FCSTD DOCUMENT  (FreeCAD 0.21R33694 (Git))
Label: boceto-carcasa
License: Creative Commons Attribution-NonCommercial-ShareAlike 4.0
LicenseURL: https://creativecommons.org/licenses/by-nc-sa/4.0/
objects: Part::Fuse×25, Part::Box×15, Part::Cut×15, Part::Feature×13, Part::Mirroring×13, Part::Cylinder×8, Sketcher::SketchObject×4, Part::Extrusion×4, Part::Chamfer×4, Part::Fillet×3, PartDesign::Body×2, Part::MultiFuse×2, App::LinkGroup×2, Mesh::Feature×1, PartDesign::Pad×1, Part::Compound×1
note: 111 computed .brp shape members not serialized (recipe doc carries the construction recipe); baked Part::Feature solids carry a one-line shape summary decoded from their .brp

FEATURE [Sketcher::SketchObject] Sketch  label="case-taladros"
  FullyConstrained = true
  MapMode = 5
  Support = -> [XY_Plane]
  sketch-geometry (8):
    g0: LineSegment StartX=-50 StartY=85 StartZ=0 EndX=50 EndY=85 EndZ=0
    g1: LineSegment StartX=50 StartY=85 StartZ=0 EndX=50 EndY=-85 EndZ=0
    g2: LineSegment StartX=50 StartY=-85 StartZ=0 EndX=-50 EndY=-85 EndZ=0
    g3: LineSegment StartX=-50 StartY=-85 StartZ=0 EndX=-50 EndY=85 EndZ=0
    g4: Circle CenterX=-40 CenterY=80 CenterZ=0 NormalX=0 NormalY=0 NormalZ=1 AngleXU=0 Radius=1.5
    g5: Circle CenterX=40 CenterY=80 CenterZ=0 NormalX=0 NormalY=0 NormalZ=1 AngleXU=0 Radius=1.5
    g6: Circle CenterX=40 CenterY=-80 CenterZ=0 NormalX=0 NormalY=0 NormalZ=1 AngleXU=0 Radius=1.5
    g7: Circle CenterX=-40 CenterY=-80 CenterZ=0 NormalX=0 NormalY=0 NormalZ=1 AngleXU=0 Radius=1.5
  constraints (19):
    c: Coincident(g0,g1)
    c: Coincident(g1,g2)
    c: Coincident(g2,g3)
    c: Coincident(g3,g0)
    c: Horizontal(g2)
    c: Vertical(g1)
    c: Symmetric(g0,g0,g-2)
    c: Symmetric(g2,g0,g-1)
    c: Equal(g4,g7)
    c: Equal(g7,g6)
    c: Equal(g6,g5)
    c: Symmetric(g7,g4,g-1)
    c: Symmetric(g4,g5,g-2)
    c: Symmetric(g6,g7,g-2)
    c: Diameter(g4) = 3
    c: DistanceY(g4,g0) = 5
    c: DistanceX(g0,g4) = 10
    c: DistanceY(g3,g3) = 170
    c: DistanceX(g0,g0) = 100
FEATURE [PartDesign::Body] Body  label="carcasa-boceto"
  Group = -> [Sketch]
  Origin = -> Origin
FEATURE [Part::Extrusion] Extrude  label="carcasa-extruida"
  Base = -> Sketch
  Dir = (0,0,1)
  DirMode = 2
  FaceMakerClass = Part::FaceMakerBullseye
  LengthFwd = 45
  LengthRev = 0
  Solid = true
  Symmetric = false
FEATURE [Part::Box] Box  label="llenado"
  AttacherType = Attacher::AttachEngine3D
  Height = 35
  Length = 100
  Placement = pos=(-50,-85,0) rot=(0,0,1;0rad)
  Width = 170
FEATURE [Part::Fuse] Fusion  label="carcasa-taladrada"
  Base = -> Extrude
  Refine = true
  Tool = -> Box
FEATURE [Part::Box] Box001  label="vaciado"
  AttacherType = Attacher::AttachEngine3D
  Height = 40
  Length = 80
  Placement = pos=(-40,-75,5) rot=(0,0,1;0rad)
  Width = 150
FEATURE [Part::Cut] Cut  label="carcasa-vaciada"
  Base = -> Fusion
  Refine = true
  Tool = -> Box001
FEATURE [Part::Fillet] Fillet
  Base = -> Cut
  Edges = 4 edges r=2: [Edge8,Edge9,Edge10,Edge11]
FEATURE [Part::Chamfer] Chamfer  label="carcasa001"
  Base = -> Fillet
  Edges = 4 edges r=2: [Edge5,Edge6,Edge7,Edge8]
FEATURE [Mesh::Feature] Arduino_Bumper_0005  label="Arduino-uno-case"
  Placement = pos=(-13,-40,5) rot=(0,0,1;-1.5708rad)
FEATURE [Part::Box] Box006  label="Cubo"
  AttacherType = Attacher::AttachEngine3D
  Height = 4
  Length = 50
  Placement = pos=(-25,22,-7.5) rot=(0,0,1;0rad)
  Width = 30
FEATURE [Part::Box] Box007  label="Cubo001"
  AttacherType = Attacher::AttachEngine3D
  Height = 20
  Length = 56
  Placement = pos=(-145,76,-21.5) rot=(0,0,1;0rad)
  Width = 16
FEATURE [Part::Cylinder] Cylinder001  label="cilindro-movil"
  Angle = 360
  AttacherType = Attacher::AttachEngine3D
  FirstAngle = 0
  Height = 170
  Placement = pos=(-200,92,-6) rot=(0,1,0;1.5708rad)
  Radius = 5
  SecondAngle = 0
FEATURE [Part::Feature] Fusion001005  label="Rosca macho006"
  Placement = pos=(-17,27,-10) rot=(0,0,1;0rad)
  shape: bbox 3.919 x 4.387 x 44 mm, 35 faces (baked)
FEATURE [Part::Feature] Fusion001006  label="Rosca macho007"
  Placement = pos=(17,27,-10) rot=(0,0,1;0rad)
  shape: bbox 3.919 x 4.387 x 44 mm, 35 faces (baked)
FEATURE [Part::MultiFuse] Fusion001007
  Refine = true
  Shapes = -> [Fusion001005,Fusion001006]
FEATURE [Part::Cut] Cut005  label="Soporte_eje"
  Base = -> Box006
  Placement = pos=(-117,36,0) rot=(0,0,1;0rad)
  Refine = true
  Tool = -> Fusion001007
FEATURE [Part::Feature] Fusion001008  label="Rosca macho008"
  Placement = pos=(-170,93.75,-8.78) rot=(0.819304,0.219813,-0.52955;0.936369rad)
  shape: bbox 4.221 x 33 x 32.52 mm, 35 faces (baked)
FEATURE [Part::Feature] Fusion001009  label="Rosca macho009"
  Placement = pos=(-60,93.75,-8.78) rot=(0.819304,0.219813,-0.52955;0.936369rad)
  shape: bbox 4.221 x 33 x 32.52 mm, 35 faces (baked)
FEATURE [Sketcher::SketchObject] Sketch007
  FullyConstrained = false
  MapMode = 5
  Placement = pos=(0,0,0) rot=(0.57735,0.57735,0.57735;2.0944rad)
  Support = -> [YZ_Plane003]
  sketch-geometry (6):
    g0: Circle CenterX=0 CenterY=0 CenterZ=0 NormalX=0 NormalY=0 NormalZ=1 AngleXU=0 Radius=8
    g1: Circle CenterX=0 CenterY=-1.19343 CenterZ=0 NormalX=0 NormalY=0 NormalZ=1 AngleXU=0 Radius=5.5
    g2: LineSegment StartX=-2.35964 StartY=6.31767 StartZ=0 EndX=2.35964 EndY=6.31767 EndZ=0
    g3: LineSegment StartX=2.35964 StartY=6.31767 StartZ=0 EndX=2.35964 EndY=5.38418 EndZ=0
    g4: LineSegment StartX=2.35964 StartY=5.38418 StartZ=0 EndX=-2.35964 EndY=5.38418 EndZ=0
    g5: LineSegment StartX=-2.35964 StartY=5.38418 StartZ=0 EndX=-2.35964 EndY=6.31767 EndZ=0
  constraints (12):
    c: Coincident(g0,g-1)
    c: Coincident(g2,g3)
    c: Coincident(g3,g4)
    c: Coincident(g4,g5)
    c: Coincident(g5,g2)
    c: Horizontal(g4)
    c: Vertical(g3)
    c: Vertical(g5)
    c: Symmetric(g2,g2,g-2)
    c: PointOnObject(g1,g-2)
    c: Radius(g0) = 8
    c: Radius(g1) = 5.5
FEATURE [PartDesign::Pad] Pad003
  Direction = (1,-2e-16,3e-16)
  Length = 170
  Length2 = 100
  Placement = pos=(0,0,0) rot=(0.57735,0.57735,0.57735;2.0944rad)
  Profile = -> Sketch007
  Refine = true
  Type = 0
FEATURE [PartDesign::Body] Body003
  Group = -> [Sketch007,Pad003]
  Origin = -> Origin003
  Placement = pos=(-200,91,-5.5) rot=(1,0,0;0.959931rad)
  Tip = -> Pad003
FEATURE [Part::Cut] Cut004
  Base = -> Body003
  Refine = true
  Tool = -> Box007
FEATURE [Part::Cut] Cut023
  Base = -> Cut004
  Refine = true
  Tool = -> Fusion001008
FEATURE [Part::Cut] Cut024  label="cilindro-fijo"
  Base = -> Cut023
  Refine = true
  Tool = -> Fusion001009
FEATURE [Part::Fuse] Fusion001010  label="ajuste-brazo"
  Base = -> Cut005
  Refine = true
  Tool = -> Cylinder001
FEATURE [Part::Fuse] Fusion001011  label="mecanismo-ajuste"
  Base = -> Cut024
  Placement = pos=(165,115,38) rot=(0,0,1;1.5708rad)
  Refine = true
  Tool = -> Fusion001010
FEATURE [Part::Feature] Wire
  Placement = pos=(-6,0,48.25) rot=(0,1,0;0.610865rad)
  shape: bbox 9.138 x 2e-07 x 16 mm, 0 faces, 0 solids (baked)
FEATURE [Part::Extrusion] Extrude001
  Base = -> Wire
  Dir = (9e-16,1,-1e-16)
  DirMode = 2
  FaceMakerClass = Part::FaceMakerBullseye
  LengthFwd = 170
  LengthRev = 0
  Placement = pos=(0.5,0,0.04) rot=(0,0,1;0rad)
  Solid = true
  Symmetric = false
FEATURE [Part::Fuse] Fusion001012  label="conex-brazo"
  Base = -> Fusion001011
  Placement = pos=(-17,0,-8) rot=(0,0,1;0rad)
  Refine = true
  Tool = -> Extrude001
FEATURE [Part::Mirroring] Part__Mirroring003  label="conex-brazo (Mirror #4)"
  Base = (0,0,0)
  Normal = (1,0,0)
  Source = -> Fusion001012
FEATURE [Sketcher::SketchObject] Sketch008  label="tapa-taladros"
  FullyConstrained = true
  MapMode = 5
  sketch-geometry (8):
    g0: LineSegment StartX=-48 StartY=83 StartZ=0 EndX=48 EndY=83 EndZ=0
    g1: LineSegment StartX=48 StartY=83 StartZ=0 EndX=48 EndY=-83 EndZ=0
    g2: LineSegment StartX=48 StartY=-83 StartZ=0 EndX=-48 EndY=-83 EndZ=0
    g3: LineSegment StartX=-48 StartY=-83 StartZ=0 EndX=-48 EndY=83 EndZ=0
    g4: Circle CenterX=-40 CenterY=80 CenterZ=0 NormalX=0 NormalY=0 NormalZ=1 AngleXU=0 Radius=0.5
    g5: Circle CenterX=40 CenterY=80 CenterZ=0 NormalX=0 NormalY=0 NormalZ=1 AngleXU=0 Radius=0.5
    g6: Circle CenterX=40 CenterY=-80 CenterZ=0 NormalX=0 NormalY=0 NormalZ=1 AngleXU=0 Radius=0.5
    g7: Circle CenterX=-40 CenterY=-80 CenterZ=0 NormalX=0 NormalY=0 NormalZ=1 AngleXU=0 Radius=0.5
  constraints (19):
    c: Coincident(g0,g1)
    c: Coincident(g1,g2)
    c: Coincident(g2,g3)
    c: Coincident(g3,g0)
    c: Horizontal(g2)
    c: Vertical(g1)
    c: Symmetric(g0,g0,g-2)
    c: Symmetric(g2,g0,g-1)
    c: Equal(g4,g7)
    c: Equal(g7,g6)
    c: Equal(g6,g5)
    c: Symmetric(g7,g4,g-1)
    c: Symmetric(g4,g5,g-2)
    c: Symmetric(g6,g7,g-2)
    c: Diameter(g4) = 1
    c: DistanceY(g4,g0) = 3
    c: DistanceX(g0,g4) = 8
    c: DistanceY(g3,g3) = 166
    c: DistanceX(g0,g0) = 96
FEATURE [Part::Extrusion] Extrude002  label="tapa"
  Base = -> Sketch008
  Dir = (0,0,1)
  DirMode = 2
  FaceMakerClass = Part::FaceMakerBullseye
  LengthFwd = 5
  LengthRev = 0
  Placement = pos=(0,0,45) rot=(0,0,1;0rad)
  Solid = true
  Symmetric = false
FEATURE [Part::Chamfer] Chamfer001  label="tapa-case"
  Base = -> Extrude002
  Edges = 4 edges r=1: [Edge4,Edge7,Edge10,Edge12]
FEATURE [Part::Cylinder] Cylinder002  label="enbellezedor-cables"
  Angle = 360
  AttacherType = Attacher::AttachEngine3D
  FirstAngle = 0
  Height = 5
  Placement = pos=(45,0,39) rot=(0,1,0;1.5708rad)
  Radius = 6
  SecondAngle = 0
FEATURE [Part::Cylinder] Cylinder003  label="enbellezedor-cables2"
  Angle = 360
  AttacherType = Attacher::AttachEngine3D
  FirstAngle = 0
  Height = 5
  Placement = pos=(-50,0,39) rot=(0,1,0;1.5708rad)
  Radius = 6
  SecondAngle = 0
FEATURE [Part::Fuse] Fusion001013  label="enbellezedores-cables"
  Base = -> Cylinder002
  Refine = true
  Tool = -> Cylinder003
FEATURE [Part::Fuse] Fusion001014  label="carcasa002"
  Base = -> Chamfer
  Refine = true
  Tool = -> Fusion001013
FEATURE [Part::Cylinder] Cylinder004  label="agujero-cables"
  Angle = 360
  AttacherType = Attacher::AttachEngine3D
  FirstAngle = 0
  Height = 20
  Placement = pos=(43,0,38) rot=(0,1,0;1.5708rad)
  Radius = 5
  SecondAngle = 0
FEATURE [Part::Mirroring] Part__Mirroring007  label="agujero-cables (Mirror #8)"
  Base = (0,0,0)
  Normal = (1,0,0)
  Source = -> Cylinder004
FEATURE [Part::Fillet] Fillet002  label="carcasa003"
  Base = -> Fusion001014
  Edges = 4 edges r=3: [Edge49,Edge54,Edge63,Edge64]
FEATURE [Part::Cylinder] Cylinder005  label="rellenados"
  Angle = 360
  AttacherType = Attacher::AttachEngine3D
  FirstAngle = 0
  Height = 10
  Placement = pos=(-40,80,35) rot=(0,0,1;0rad)
  Radius = 1.5
  SecondAngle = 0
FEATURE [Part::Mirroring] Part__Mirroring008  label="rellenados (Mirror #9)"
  Base = (0,0,0)
  Normal = (1,0,0)
  Source = -> Cylinder005
FEATURE [Part::Fuse] Fusion001015  label="rellenados-1"
  Base = -> Cylinder005
  Refine = true
  Tool = -> Part__Mirroring008
FEATURE [Part::Cylinder] Cylinder006  label="rellenados001"
  Angle = 360
  AttacherType = Attacher::AttachEngine3D
  FirstAngle = 0
  Height = 10
  Placement = pos=(-40,80,35) rot=(0,0,1;0rad)
  Radius = 1.5
  SecondAngle = 0
FEATURE [Part::Mirroring] Part__Mirroring009  label="rellenados (Mirror #9)001"
  Base = (0,0,0)
  Normal = (1,0,0)
  Source = -> Cylinder006
FEATURE [Part::Fuse] Fusion001016  label="rellenados-2"
  Base = -> Cylinder006
  Placement = pos=(0,-160,0) rot=(0,0,1;0rad)
  Refine = true
  Tool = -> Part__Mirroring009
FEATURE [Part::Fuse] Fusion001017  label="rellenados002"
  Base = -> Fusion001015
  Refine = true
  Tool = -> Fusion001016
FEATURE [Part::Fuse] Fusion001018  label="carcasa004"
  Base = -> Fillet002
  Refine = true
  Tool = -> Fusion001017
FEATURE [Part::Feature] Fusion001001  label="Rosca macho002"
  Placement = pos=(40,-80,60) rot=(0,0,1;0rad)
  shape: bbox 3.919 x 4.387 x 44 mm, 35 faces (baked)
FEATURE [Part::Mirroring] Part__Mirroring004  label="Rosca macho002 (Mirror #5)"
  Base = (0,0,0)
  Normal = (1,0,0)
  Source = -> Fusion001001
FEATURE [Part::Mirroring] Part__Mirroring005  label="Rosca macho002 (Mirror #6)"
  Base = (0,0,0)
  Normal = (0,1,0)
  Source = -> Part__Mirroring004
FEATURE [Part::Mirroring] Part__Mirroring006  label="Rosca macho002 (Mirror #7)"
  Base = (0,0,0)
  Normal = (1,0,0)
  Source = -> Part__Mirroring005
FEATURE [Part::Fuse] Fusion001019
  Base = -> Part__Mirroring005
  Refine = true
  Tool = -> Part__Mirroring006
FEATURE [Part::Fuse] Fusion001020
  Base = -> Fusion001001
  Refine = true
  Tool = -> Part__Mirroring004
FEATURE [Part::Fuse] Fusion001021  label="roscas"
  Base = -> Fusion001019
  Placement = pos=(0,0,-24) rot=(0,0,1;0rad)
  Refine = true
  Tool = -> Fusion001020
FEATURE [Part::Feature] Fusion001022  label="Rosca macho010"
  Placement = pos=(40,-80,60) rot=(0,0,1;0rad)
  shape: bbox 3.919 x 4.387 x 44 mm, 35 faces (baked)
FEATURE [Part::Mirroring] Part__Mirroring010  label="Rosca macho002 (Mirror #5)001"
  Base = (0,0,0)
  Normal = (1,0,0)
  Source = -> Fusion001022
FEATURE [Part::Fuse] Fusion001024
  Base = -> Fusion001022
  Refine = true
  Tool = -> Part__Mirroring010
FEATURE [Part::Mirroring] Part__Mirroring011  label="Rosca macho002 (Mirror #6)001"
  Base = (0,0,0)
  Normal = (0,1,0)
  Source = -> Part__Mirroring010
FEATURE [Part::Mirroring] Part__Mirroring012  label="Rosca macho002 (Mirror #7)001"
  Base = (0,0,0)
  Normal = (1,0,0)
  Source = -> Part__Mirroring011
FEATURE [Part::Fuse] Fusion001023
  Base = -> Part__Mirroring011
  Refine = true
  Tool = -> Part__Mirroring012
FEATURE [Part::Fuse] Fusion001025  label="roscas001"
  Base = -> Fusion001023
  Placement = pos=(0,0,-24) rot=(0,0,1;0rad)
  Refine = true
  Tool = -> Fusion001024
FEATURE [Part::Cut] Cut025  label="tapa-roscada"
  Base = -> Chamfer001
  Placement = pos=(0,0,45) rot=(0,0,1;0rad)
  Refine = true
  Tool = -> Fusion001021
FEATURE [Part::Cut] Cut026  label="carcasa-roscada"
  Base = -> Fusion001018
  Refine = true
  Tool = -> Fusion001025
FEATURE [Part::Box] Box008  label="Cube"
  AttacherType = Attacher::AttachEngine3D
  Height = 5
  Length = 10
  Width = 20
FEATURE [Part::Box] Box009  label="Cube001"
  AttacherType = Attacher::AttachEngine3D
  Height = 50
  Length = 5
  Placement = pos=(-5,0,0) rot=(0,0,1;0rad)
  Width = 20
FEATURE [Part::Box] Box002  label="Cube002"
  AttacherType = Attacher::AttachEngine3D
  Height = 50
  Length = 5
  Placement = pos=(-5,0,0) rot=(0,0,1;0rad)
  Width = 20
FEATURE [Part::Box] Box003  label="Cube003"
  AttacherType = Attacher::AttachEngine3D
  Height = 20
  Length = 10
  Placement = pos=(0,5,5) rot=(0,0,1;0rad)
  Width = 10
FEATURE [Part::Cylinder] Cylinder
  Angle = 360
  AttacherType = Attacher::AttachEngine3D
  FirstAngle = 0
  Height = 6
  Placement = pos=(5,10,0) rot=(0,0,1;0rad)
  Radius = 0.5
  SecondAngle = 0
FEATURE [Part::Fuse] Fusion001026
  Base = -> Box008
  Refine = true
  Tool = -> Box009
FEATURE [Part::Fillet] Fillet003
  Base = -> Fusion001026
  Edges = 1 edges r=9.99: [Edge5]
FEATURE [Part::Cut] Cut027
  Base = -> Fillet003
  Refine = true
  Tool = -> Box002
FEATURE [Part::Cut] Cut001
  Base = -> Cut027
  Refine = true
  Tool = -> Box003
FEATURE [Part::Cut] Cut002  label="acople"
  Base = -> Cut001
  Refine = true
  Tool = -> Cylinder
FEATURE [Part::Feature] Fusion001027  label="Rosca macho011"
  Placement = pos=(5,10,-9) rot=(0,0,1;0rad)
  shape: bbox 3.919 x 4.387 x 44 mm, 35 faces (baked)
FEATURE [Part::Cut] Cut003  label="acople-roscado"
  Base = -> Cut002
  Placement = pos=(50,-85,5) rot=(0,0,1;0rad)
  Refine = true
  Tool = -> Fusion001027
FEATURE [Part::Mirroring] Part__Mirroring  label="acople-roscado (Mirror #11)"
  Base = (0,0,0)
  Normal = (1,0,0)
  Source = -> Cut003
FEATURE [Part::Fuse] Fusion001028
  Base = -> Cut003
  Refine = true
  Tool = -> Part__Mirroring
FEATURE [Part::Mirroring] Part__Mirroring013  label="Fusion001028 (Mirror #12)"
  Base = (0,0,0)
  Normal = (0,1,0)
  Source = -> Fusion001028
FEATURE [Part::Fuse] Fusion001029  label="acoples-flotador"
  Base = -> Fusion001028
  Refine = true
  Tool = -> Part__Mirroring013
FEATURE [Part::Fuse] Fusion001030  label="agujeros-cables"
  Base = -> Cylinder004
  Refine = true
  Tool = -> Part__Mirroring007
FEATURE [Part::Fuse] Fusion001031  label="brazos-v1"
  Base = -> Fusion001012
  Refine = true
  Tool = -> Part__Mirroring003
FEATURE [Part::Box] Box010  label="restriccion-lipo"
  AttacherType = Attacher::AttachEngine3D
  Height = 38
  Length = 5
  Placement = pos=(17,-75,5) rot=(0,0,1;0rad)
  Width = 73
FEATURE [Part::Box] Box011  label="restriccion-lipo001"
  AttacherType = Attacher::AttachEngine3D
  Height = 18
  Length = 7
  Placement = pos=(16,-60,14) rot=(0,0,1;0rad)
  Width = 43
FEATURE [Part::Cut] Cut028
  Base = -> Box010
  Refine = true
  Tool = -> Box011
FEATURE [Part::Chamfer] Chamfer002
  Base = -> Cut028
  Edges = 2 edges r=3: [Edge2,Edge4]
FEATURE [Part::Chamfer] Chamfer003
  Base = -> Chamfer002
  Edges = 4 edges r=2: [Edge5,Edge6,Edge7,Edge8]
FEATURE [Part::Box] Box012  label="Cube004"
  AttacherType = Attacher::AttachEngine3D
  Height = 5
  Length = 20
  Placement = pos=(20,-4,16) rot=(0,0,1;0rad)
  Width = 2
FEATURE [Part::Fuse] Fusion001032  label="rejillas-lipo"
  Base = -> Chamfer003
  Refine = true
  Tool = -> Box012
FEATURE [Part::Box] Box013  label="PDB-space"
  AttacherType = Attacher::AttachEngine3D
  Height = 3
  Length = 36
  Placement = pos=(0,19,9.5) rot=(0,0,1;0rad)
  Width = 56
FEATURE [Part::Feature] Compound001  label="pcb-support"
  Placement = pos=(18,53,5) rot=(0,0,1;3.14159rad)
  shape: bbox 40 x 56.1 x 12 mm, 27565 faces, 3 solids (baked)
FEATURE [Part::Box] Box014  label="protoboard-space"
  AttacherType = Attacher::AttachEngine3D
  Height = 40
  Length = 38
  Placement = pos=(-40,-5,5) rot=(0,0,1;0rad)
  Width = 80
FEATURE [Part::Box] Box015  label="Cubo002"
  AttacherType = Attacher::AttachEngine3D
  Height = 4
  Length = 50
  Placement = pos=(-25,22,-7.5) rot=(0,0,1;0rad)
  Width = 30
FEATURE [Part::Box] Box016  label="cubo-corte"
  AttacherType = Attacher::AttachEngine3D
  Height = 20
  Length = 56
  Placement = pos=(-145,75,-20) rot=(0,0,1;0rad)
  Width = 16
FEATURE [Part::Cylinder] Cylinder007  label="Cilindro-movil"
  Angle = 360
  AttacherType = Attacher::AttachEngine3D
  FirstAngle = 0
  Height = 170
  Placement = pos=(-200,92,-6) rot=(0,1,0;1.5708rad)
  Radius = 3.5
  SecondAngle = 0
FEATURE [Part::Feature] Fusion001034  label="Rosca macho012"
  Placement = pos=(-17,27,-10) rot=(0,0,1;0rad)
  shape: bbox 3.919 x 4.387 x 44 mm, 35 faces (baked)
FEATURE [Part::Feature] Fusion001035  label="Rosca macho013"
  Placement = pos=(17,27,-10) rot=(0,0,1;0rad)
  shape: bbox 3.919 x 4.387 x 44 mm, 35 faces (baked)
FEATURE [Part::MultiFuse] Fusion001036
  Refine = true
  Shapes = -> [Fusion001034,Fusion001035]
FEATURE [Part::Cut] Cut030  label="Soporte_eje001"
  Base = -> Box015
  Placement = pos=(-117,38,0) rot=(0,0,1;0rad)
  Refine = true
  Tool = -> Fusion001036
FEATURE [Part::Feature] Fusion001037  label="Rosca macho014"
  Placement = pos=(-170,93.75,-8.78) rot=(0.819304,0.219813,-0.52955;0.936369rad)
  shape: bbox 4.221 x 33 x 32.52 mm, 35 faces (baked)
FEATURE [Part::Feature] Fusion001038  label="Rosca macho015"
  Placement = pos=(-60,93.75,-8.78) rot=(0.819304,0.219813,-0.52955;0.936369rad)
  shape: bbox 4.221 x 33 x 32.52 mm, 35 faces (baked)
FEATURE [Part::Fuse] Fusion001033  label="roscas002"
  Base = -> Fusion001037
  Refine = true
  Tool = -> Fusion001038
FEATURE [Part::Fuse] Fusion001039  label="cilindro-movil001"
  Base = -> Cut030
  Refine = true
  Tool = -> Cylinder007
FEATURE [Sketcher::SketchObject] Sketch009
  FullyConstrained = false
  MapMode = 5
  Placement = pos=(0,0,0) rot=(0.57735,0.57735,0.57735;2.0944rad)
  Support = -> [YZ_Plane004]
  sketch-geometry (9):
    g0: ArcOfCircle CenterX=0 CenterY=0 CenterZ=0 NormalX=0 NormalY=0 NormalZ=1 AngleXU=0 Radius=5.5 StartAngle=6.08579 EndAngle=9.70025
    g1: Circle CenterX=0 CenterY=-1.19343 CenterZ=0 NormalX=0 NormalY=0 NormalZ=1 AngleXU=0 Radius=4
    g2: LineSegment StartX=-2.36 StartY=4.37566 StartZ=0 EndX=2.36 EndY=4.37566 EndZ=0
    g3: LineSegment StartX=2.36 StartY=4.37566 StartZ=0 EndX=2.36 EndY=3.44566 EndZ=0
    g4: LineSegment StartX=2.36 StartY=3.44566 StartZ=0 EndX=-2.36 EndY=3.44566 EndZ=0
    g5: LineSegment StartX=-2.36 StartY=3.44566 StartZ=0 EndX=-2.36 EndY=4.37566 EndZ=0
    g6: LineSegment StartX=-5.29263 StartY=-1.49602 StartZ=0 EndX=-5.29263 EndY=-8 EndZ=0
    g7: LineSegment StartX=-5.29263 StartY=-8 StartZ=0 EndX=5.39319 EndY=-8 EndZ=0
    g8: LineSegment StartX=5.39319 StartY=-8 StartZ=0 EndX=5.39319 EndY=-1.07864 EndZ=0
  constraints (21):
    c: Coincident(g0,g-1)
    c: Coincident(g2,g3)
    c: Coincident(g3,g4)
    c: Coincident(g4,g5)
    c: Coincident(g5,g2)
    c: Horizontal(g4)
    c: Vertical(g3)
    c: Vertical(g5)
    c: Symmetric(g2,g2,g-2)
    c: PointOnObject(g1,g-2)
    c: Radius(g0) = 5.5
    c: Radius(g1) = 4
    c: DistanceY(g5,g5) = 0.93
    c: DistanceX(g2,g2) = 4.72
    c: Coincident(g6,g7)
    c: Coincident(g7,g8)
    c: Horizontal(g7)
    c: Vertical(g6)
    c: Vertical(g8)
    c: Coincident(g0,g8)
    c: Coincident(g6,g0)
FEATURE [Part::Extrusion] Extrude003  label="cilindro-fijo001"
  Base = -> Sketch009
  Dir = (1,-1e-16,1e-16)
  DirMode = 2
  FaceMakerClass = Part::FaceMakerBullseye
  LengthFwd = 170
  LengthRev = 0
  Placement = pos=(-200,91,-5) rot=(1,0,0;1.02974rad)
  Solid = true
  Symmetric = false
FEATURE [Part::Cut] Cut029
  Base = -> Extrude003
  Refine = true
  Tool = -> Fusion001033
FEATURE [Part::Cut] Cut031  label="fijacion-brazo"
  Base = -> Cut029
  Refine = true
  Tool = -> Box016
FEATURE [Part::Compound] Compound  label="brazo-mejorados"
  Links = -> [Cut031,Fusion001039]
  Placement = pos=(136,115,-16.54) rot=(0.26,0.26,0.93;1.64236rad)
FEATURE [Part::Mirroring] Part__Mirroring014  label="brazo-mejorados (Mirror #13)"
  Base = (0,0,0)
  Normal = (1,0,0)
  Source = -> Compound
FEATURE [Part::Fuse] Fusion001040  label="brazos-v2"
  Base = -> Compound
  Refine = true
  Tool = -> Part__Mirroring014
FEATURE [App::LinkGroup] LinkGroup  label="componentes-shell"
  ElementList = -> [Compound001,Box013,Box014,Fusion001032,Arduino_Bumper_0005]
  LinkMode = 0
FEATURE [App::LinkGroup] LinkGroup001  label="brazos"
  ElementList = -> [Fusion001031,Fusion001040]
  LinkMode = 0
